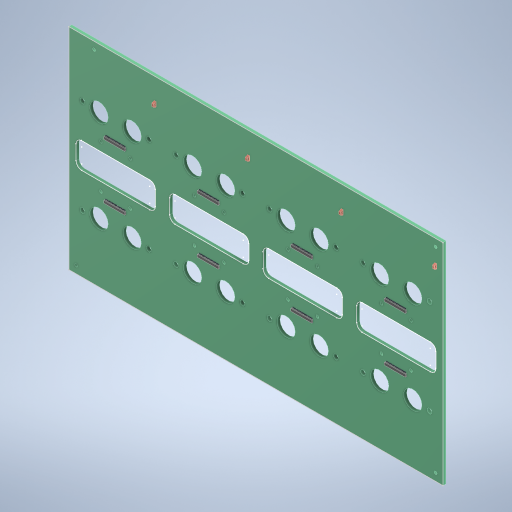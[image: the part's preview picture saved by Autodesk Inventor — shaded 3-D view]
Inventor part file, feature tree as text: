
AUTODESK INVENTOR PART (.ipt)
format: ipt  version: 2023 (Build 270158000, 158)  size: 2,038,784 bytes
history: native  units: in
note: dims shown in document units (in); Inventor stores cm internally (conversion verified against a paired STEP export)
features: sketch x6, other x1, extrude x1
ambient origin geometry x8: Origin, YZ Plane, XZ Plane, XY Plane, X Axis, Y Axis, Z Axis, Center Point
bodies: Solid1 (feature_tree), Solid2 (feature_tree), Solid3 (feature_tree), Solid4 (feature_tree), Solid5 (feature_tree), Solid6 (feature_tree), Solid7 (feature_tree), Solid8 (feature_tree), Solid9 (feature_tree), Solid10 (feature_tree), Solid11 (feature_tree), Solid12 (feature_tree), Solid13 (feature_tree), Solid14 (feature_tree), Solid15 (feature_tree), Solid16 (feature_tree), Solid17 (feature_tree), Solid18 (feature_tree), Solid19 (feature_tree), Solid20 (feature_tree), Solid21 (feature_tree), Solid22 (feature_tree), Solid23 (feature_tree), Solid24 (feature_tree), Solid25 (feature_tree), Solid26 (feature_tree), Solid27 (feature_tree), Solid28 (feature_tree), Solid29 (feature_tree), Solid30 (feature_tree), Solid31 (feature_tree), Solid32 (feature_tree), Solid33 (feature_tree), Solid34 (feature_tree), Solid35 (feature_tree), Solid36 (feature_tree), Solid37 (feature_tree), Solid38 (feature_tree), Solid39 (feature_tree), Solid40 (feature_tree), Solid41 (feature_tree), Solid42 (feature_tree), Solid43 (feature_tree), Solid44 (feature_tree), Solid45 (feature_tree), Solid46 (feature_tree), Solid47 (feature_tree), Solid48 (feature_tree), Solid49 (feature_tree), Solid50 (feature_tree), Solid51 (feature_tree), Solid52 (feature_tree), Solid53 (feature_tree), Solid54 (feature_tree), Solid55 (feature_tree), Solid56 (feature_tree), Solid57 (feature_tree), Solid58 (feature_tree), Solid59 (feature_tree), Solid60 (feature_tree), Solid61 (feature_tree), Solid62 (feature_tree), Solid63 (feature_tree), Solid64 (feature_tree), Solid65 (feature_tree), Solid66 (feature_tree), Solid67 (feature_tree), Solid68 (feature_tree), Solid69 (feature_tree), Solid70 (feature_tree), Solid71 (feature_tree), Solid72 (feature_tree), Solid73 (feature_tree), Solid74 (feature_tree), Solid75 (feature_tree), Solid76 (feature_tree), Solid77 (feature_tree), Solid78 (feature_tree), Solid79 (feature_tree), Solid80 (feature_tree), Solid81 (feature_tree), Solid82 (feature_tree), Solid83 (feature_tree), Solid84 (feature_tree), Solid85 (feature_tree), Solid86 (feature_tree), Solid87 (feature_tree), Solid88 (feature_tree), Solid89 (feature_tree), Solid90 (feature_tree), Solid91 (feature_tree), Solid92 (feature_tree), Solid93 (feature_tree), Solid94 (feature_tree), Solid95 (feature_tree), Solid96 (feature_tree), Solid97 (feature_tree), Solid98 (feature_tree), Solid99 (feature_tree), Solid100 (feature_tree), Solid101 (feature_tree), Solid102 (feature_tree), Solid103 (feature_tree), Solid104 (feature_tree), Solid105 (feature_tree), Solid106 (feature_tree), Solid107 (feature_tree), Solid108 (feature_tree), Solid109 (feature_tree), Solid110 (feature_tree), Solid111 (feature_tree), Solid112 (feature_tree), Solid113 (feature_tree), Solid114 (feature_tree), Solid115 (feature_tree), Solid116 (feature_tree), Solid117 (feature_tree), Solid118 (feature_tree), Solid119 (feature_tree), Solid120 (feature_tree), Solid121 (feature_tree), Solid122 (feature_tree), Solid123 (feature_tree), Solid124 (feature_tree), Solid125 (feature_tree), Solid126 (feature_tree), Solid127 (feature_tree), Solid128 (feature_tree), Solid129 (feature_tree), Solid130 (feature_tree), Solid131 (feature_tree), Solid132 (feature_tree), Solid133 (feature_tree), Solid134 (feature_tree), Solid135 (feature_tree), Solid136 (feature_tree), Solid137 (feature_tree), Solid138 (feature_tree), Solid139 (feature_tree), Solid140 (feature_tree), Solid141 (feature_tree), Solid142 (feature_tree), Solid143 (feature_tree), Solid144 (feature_tree), Solid145 (feature_tree), Solid146 (feature_tree), Solid147 (feature_tree), Solid148 (feature_tree), Solid149 (feature_tree), Solid150 (feature_tree), Solid151 (feature_tree), Solid152 (feature_tree), Solid153 (feature_tree), Solid154 (feature_tree), Solid155 (feature_tree), Solid156 (feature_tree), Solid157 (feature_tree), Solid158 (feature_tree), Solid159 (feature_tree), Solid160 (feature_tree), Solid161 (feature_tree), Solid162 (feature_tree), Solid163 (feature_tree), Solid164 (feature_tree), Solid165 (feature_tree), Solid166 (feature_tree), Solid167 (feature_tree), Solid168 (feature_tree), Solid169 (feature_tree), Solid170 (feature_tree), Solid171 (feature_tree), Solid172 (feature_tree), Solid173 (feature_tree), Solid174 (feature_tree), Solid175 (feature_tree), Solid176 (feature_tree), Solid177 (feature_tree), Solid178 (feature_tree), Solid179 (feature_tree), Solid180 (feature_tree), Solid181 (feature_tree), Solid182 (feature_tree), Solid183 (feature_tree), Solid184 (feature_tree), Solid185 (feature_tree), Solid186 (feature_tree), Solid187 (feature_tree), Solid188 (feature_tree), Solid189 (feature_tree), Solid190 (feature_tree), Solid191 (feature_tree), Solid192 (feature_tree), Solid193 (feature_tree), Solid194 (feature_tree), Solid195 (feature_tree), Solid196 (feature_tree), Solid197 (feature_tree), Solid198 (feature_tree), Solid199 (feature_tree), Solid200 (feature_tree), Solid201 (feature_tree), Solid202 (feature_tree), Solid203 (feature_tree), Solid204 (feature_tree), Solid205 (feature_tree), Solid206 (feature_tree), Solid207 (feature_tree), Solid208 (feature_tree), Solid209 (feature_tree), Solid210 (feature_tree), Solid211 (feature_tree), Solid212 (feature_tree), Solid213 (feature_tree), Solid214 (feature_tree), Solid215 (feature_tree), Solid216 (feature_tree), Solid217 (feature_tree), Solid218 (feature_tree), Solid219 (feature_tree), Solid220 (feature_tree), Solid221 (feature_tree), Solid222 (feature_tree), Solid223 (feature_tree), Solid224 (feature_tree), Solid225 (feature_tree), Solid226 (feature_tree), Solid227 (feature_tree), Solid228 (feature_tree), Solid229 (feature_tree), Solid230 (feature_tree), Solid231 (feature_tree), Solid232 (feature_tree), Solid233 (feature_tree), Solid234 (feature_tree), Solid235 (feature_tree), Solid236 (feature_tree), Solid237 (feature_tree), Solid238 (feature_tree), Solid239 (feature_tree), Solid240 (feature_tree), Solid241 (feature_tree), Solid242 (feature_tree), Solid243 (feature_tree), Solid244 (feature_tree), Solid245 (feature_tree), Solid246 (feature_tree), Solid247 (feature_tree), Solid248 (feature_tree), Solid249 (feature_tree), Solid250 (feature_tree), Solid251 (feature_tree), Solid252 (feature_tree), Solid253 (feature_tree), Solid254 (feature_tree), Solid255 (feature_tree), Solid256 (feature_tree), Solid257 (feature_tree), Solid258 (feature_tree), Solid259 (feature_tree), Solid260 (feature_tree), Solid261 (feature_tree), Solid262 (feature_tree), Solid263 (feature_tree), Solid264 (feature_tree), Solid265 (feature_tree), Solid266 (feature_tree), Solid267 (feature_tree), Solid268 (feature_tree), Solid269 (feature_tree), Solid270 (feature_tree), Solid271 (feature_tree), Solid272 (feature_tree), Solid273 (feature_tree), Solid274 (feature_tree), Solid275 (feature_tree), Solid276 (feature_tree), Solid277 (feature_tree), Solid278 (feature_tree), Solid279 (feature_tree), Solid280 (feature_tree), Solid281 (feature_tree), Solid282 (feature_tree), Solid283 (feature_tree), Solid284 (feature_tree), Solid285 (feature_tree), Solid286 (feature_tree), Solid287 (feature_tree), Solid288 (feature_tree), Solid289 (feature_tree), Solid290 (feature_tree), Solid291 (feature_tree), Solid292 (feature_tree), Solid293 (feature_tree), Solid294 (feature_tree), Solid295 (feature_tree), Solid296 (feature_tree), Solid297 (feature_tree), Solid298 (feature_tree), Solid299 (feature_tree), Solid300 (feature_tree), Solid301 (feature_tree), Solid302 (feature_tree), Solid303 (feature_tree), Solid304 (feature_tree), Solid305 (feature_tree), Solid306 (feature_tree), Solid307 (feature_tree), Solid308 (feature_tree), Solid309 (feature_tree), Solid310 (feature_tree), Solid311 (feature_tree), Solid312 (feature_tree), Solid313 (feature_tree), Solid314 (feature_tree), Solid315 (feature_tree), Solid316 (feature_tree), Solid317 (feature_tree), Solid318 (feature_tree), Solid319 (feature_tree), Solid320 (feature_tree), Solid321 (feature_tree), Solid322 (feature_tree), Solid323 (feature_tree), Solid324 (feature_tree), Solid325 (feature_tree), Solid326 (feature_tree), Solid327 (feature_tree), Solid328 (feature_tree), Solid329 (feature_tree), Solid330 (feature_tree), Solid331 (feature_tree), Solid332 (feature_tree), Solid333 (feature_tree), Solid334 (feature_tree), Solid335 (feature_tree), Solid336 (feature_tree), Solid337 (feature_tree), Solid338 (feature_tree), Solid339 (feature_tree), Solid340 (feature_tree), Solid341 (feature_tree), Solid342 (feature_tree), Solid343 (feature_tree), Solid344 (feature_tree), Solid345 (feature_tree), Solid346 (feature_tree), Solid347 (feature_tree), Solid348 (feature_tree), Solid349 (feature_tree), Solid350 (feature_tree), Solid351 (feature_tree), Solid352 (feature_tree), Solid353 (feature_tree), Solid354 (feature_tree), Solid355 (feature_tree), Solid356 (feature_tree), Solid357 (feature_tree), Solid358 (feature_tree), Solid359 (feature_tree), Solid360 (feature_tree), Solid361 (feature_tree), Solid362 (feature_tree), Solid363 (feature_tree), Solid364 (feature_tree), Solid365 (feature_tree), Solid366 (feature_tree), Solid367 (feature_tree), Solid368 (feature_tree), Solid369 (feature_tree), Solid370 (feature_tree), Solid371 (feature_tree), Solid372 (feature_tree), Solid373 (feature_tree), Solid374 (feature_tree), Solid375 (feature_tree), Solid376 (feature_tree), Solid377 (feature_tree), Solid378 (feature_tree), Solid379 (feature_tree), Solid380 (feature_tree), Solid381 (feature_tree), Solid382 (feature_tree), Solid383 (feature_tree), Solid384 (feature_tree), Solid385 (feature_tree), Solid386 (feature_tree), Solid387 (feature_tree), Solid388 (feature_tree), Solid389 (feature_tree), Solid390 (feature_tree), Solid391 (feature_tree), Solid392 (feature_tree), Solid393 (feature_tree), Solid394 (feature_tree), Solid395 (feature_tree), Solid396 (feature_tree), Solid397 (feature_tree), Solid398 (feature_tree), Solid399 (feature_tree), Solid400 (feature_tree), Solid401 (feature_tree), Solid402 (feature_tree), Solid403 (feature_tree), Solid404 (feature_tree), Solid405 (feature_tree), Solid406 (feature_tree), Solid407 (feature_tree), Solid408 (feature_tree), Solid409 (feature_tree), Solid410 (feature_tree), Solid411 (feature_tree), Solid412 (feature_tree), Solid413 (feature_tree), Solid414 (feature_tree), Solid415 (feature_tree), Solid416 (feature_tree), Solid417 (feature_tree), Solid418 (feature_tree), Solid419 (feature_tree), Solid420 (feature_tree), Solid421 (feature_tree), Solid422 (feature_tree), Solid423 (feature_tree), Solid424 (feature_tree), Solid425 (feature_tree), Solid426 (feature_tree), Solid427 (feature_tree), Solid428 (feature_tree), Solid429 (feature_tree), Solid430 (feature_tree), Solid431 (feature_tree), Solid432 (feature_tree), Solid433 (feature_tree), Solid434 (feature_tree), Solid435 (feature_tree), Solid436 (feature_tree), Solid437 (feature_tree), Solid438 (feature_tree), Solid439 (feature_tree), Solid440 (feature_tree), Solid441 (feature_tree), Solid442 (feature_tree), Solid443 (feature_tree), Solid444 (feature_tree), Solid445 (feature_tree)
feature tree (8):
  other  "Repaired Geometry1"
  sketch  "3D Sketch1"
  sketch  "3D Sketch2"
  sketch  "3D Sketch3"
  sketch  "3D Sketch4"
  extrude  "Extrusion1"  Depth=0.3937in
  sketch  "3D Sketch5"
  sketch  "Sketch1"  dims[d0=0.0in d1=0.0in d8=0.3937in d9=0.3937in d11=1.2657in d12=0.7087in d14=1.4213in d15=0.3563in d16=1.5748in d18=2.0in d19=0.3937in d21=0.3937in d23=4.5in d24=2.25in]
